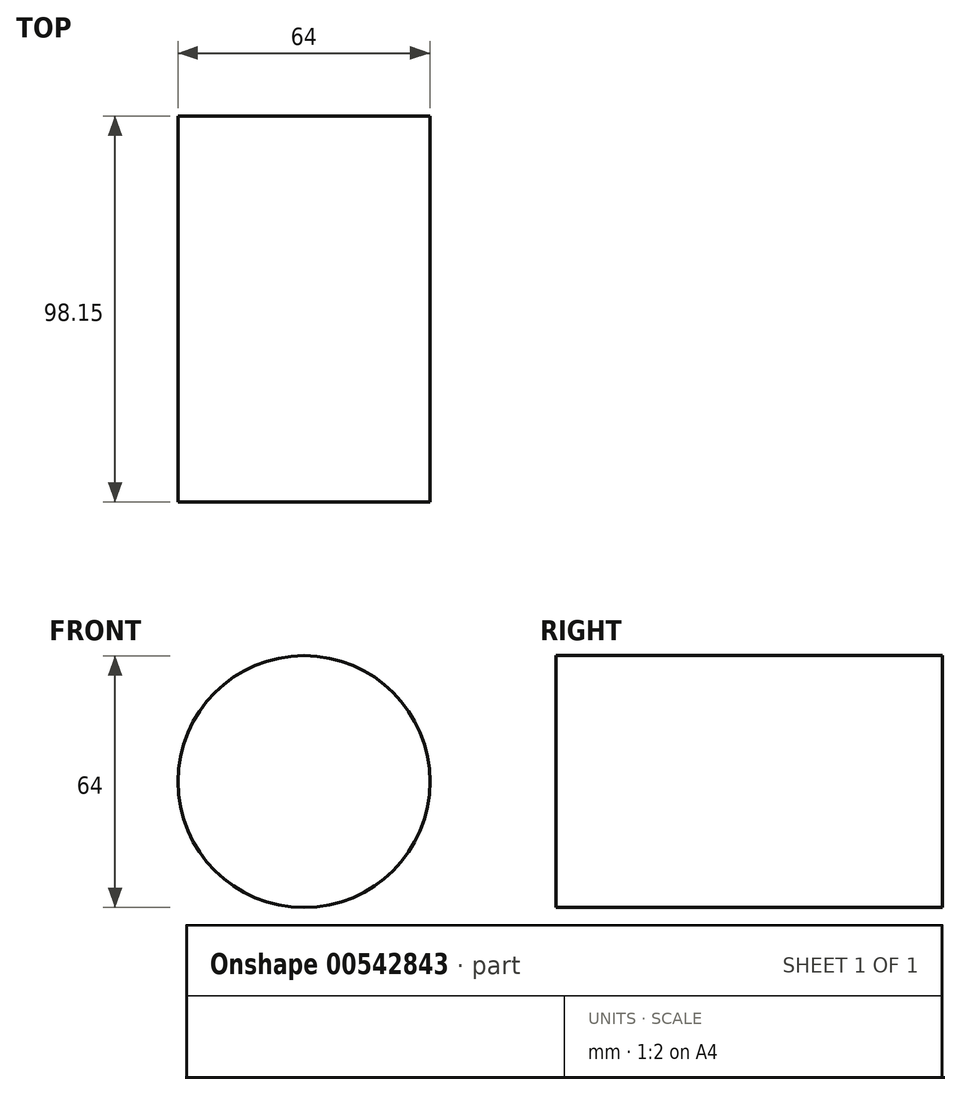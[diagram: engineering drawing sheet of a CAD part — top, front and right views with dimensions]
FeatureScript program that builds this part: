
annotation { "Feature Type Name" : "Feature", "Feature Type Description" : "" }
export const myFeature = defineFeature(function(context is Context, id is Id, definition is map)
    precondition{}
    {
        {
            var Q0;
            Q0=qCreatedBy(makeId("Front.planeOp"),FACE);
            var sketch = newSketch(context, id + "F0", { "sketchPlane" : qUnion([Q0])});
            skCircle(sketch, "E0", {"center": v(0, 0) * mm, "radius": 32 * mm});
            skSolve(sketch);
        }
        {
            var Q0;
            Q0=makeQuery(id+"F0.imprint","IMPRINT",FACE,{"disambiguationData":[TD([[makeQuery(id+"F0.imprint","IMPRINT",EDGE,{"derivedFrom":sQuery(id+"F0.wireOp",EDGE,"E0")}),1.0]])]});
            extrude(context, id + "F1", {"entities" : qUnion([Q0]), "depth" : 98.15 * mm});
        }
    });
